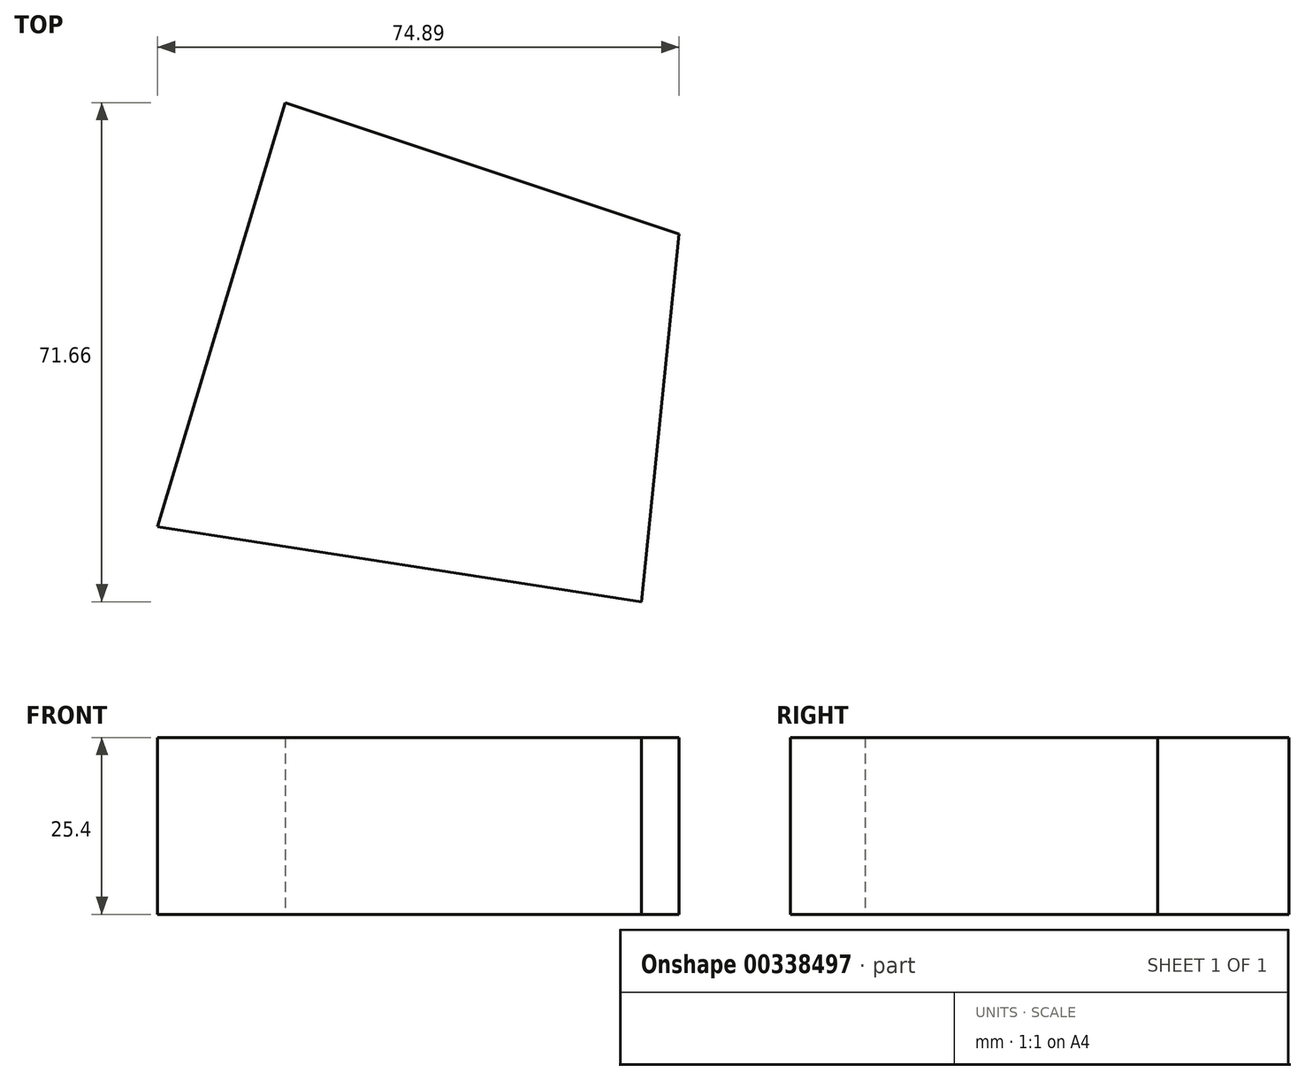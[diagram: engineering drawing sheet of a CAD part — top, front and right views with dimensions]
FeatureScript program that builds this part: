
annotation { "Feature Type Name" : "Feature", "Feature Type Description" : "" }
export const myFeature = defineFeature(function(context is Context, id is Id, definition is map)
    precondition{}
    {
        {
            var Q0;
            Q0=qCreatedBy(makeId("Top.planeOp"),FACE);
            var sketch = newSketch(context, id + "F0", { "sketchPlane" : qUnion([Q0])});
            skLineSegment(sketch, "E0", {"start": v(-25.6, 36.1) * mm, "end": v(-43.91, -24.78) * mm});
            skLineSegment(sketch, "E1", {"start": v(-43.91, -24.78) * mm, "end": v(25.6, -35.56) * mm});
            skLineSegment(sketch, "E2", {"start": v(25.6, -35.56) * mm, "end": v(30.98, 17.24) * mm});
            skLineSegment(sketch, "E3", {"start": v(30.98, 17.24) * mm, "end": v(-25.6, 36.1) * mm});
            skSolve(sketch);
        }
        {
            var Q0;
            Q0=makeQuery(id+"F0.imprint","IMPRINT",FACE,{"disambiguationData":[TD([[makeQuery(id+"F0.imprint","IMPRINT",EDGE,{"derivedFrom":sQuery(id+"F0.wireOp",EDGE,"E0")}),1.0]])]});
            extrude(context, id + "F1", {"entities" : qUnion([Q0]), "depth" : 25.4 * mm});
        }
    });
